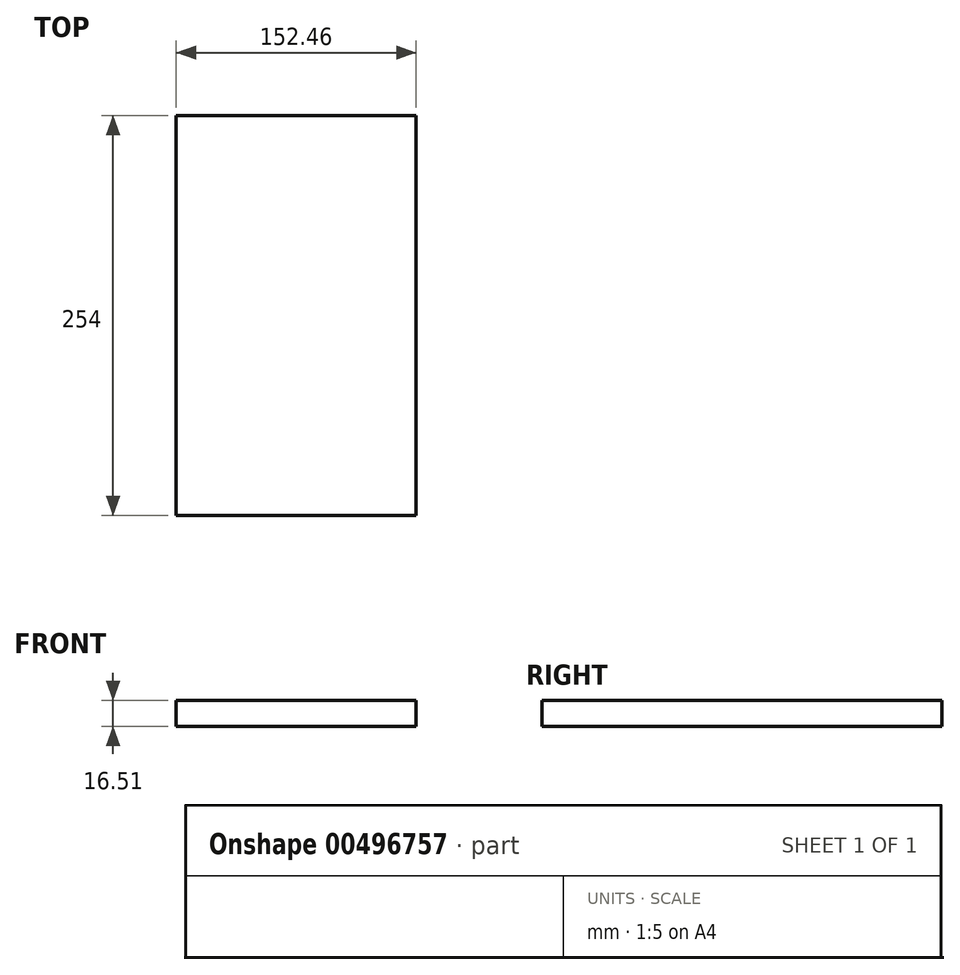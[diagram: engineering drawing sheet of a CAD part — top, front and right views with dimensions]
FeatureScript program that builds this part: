
annotation { "Feature Type Name" : "Feature", "Feature Type Description" : "" }
export const myFeature = defineFeature(function(context is Context, id is Id, definition is map)
    precondition{}
    {
        {
            var Q0;
            Q0=qCreatedBy(makeId("Front.planeOp"),FACE);
            var sketch = newSketch(context, id + "F0", { "sketchPlane" : qUnion([Q0])});
            skLineSegment(sketch, "E0", {"start": v(-76.65, 0) * mm, "end": v(-76.65, 16.5) * mm});
            skLineSegment(sketch, "E1", {"start": v(-76.65, 16.5) * mm, "end": v(75.81, 16.5) * mm});
            skLineSegment(sketch, "E2", {"start": v(75.81, 16.5) * mm, "end": v(75.81, 0) * mm});
            skLineSegment(sketch, "E3", {"start": v(75.81, 0) * mm, "end": v(-76.65, 0) * mm});
            skSolve(sketch);
        }
        {
            var Q0;
            Q0=makeQuery(id+"F0.imprint","IMPRINT",FACE,{"disambiguationData":[TD([[makeQuery(id+"F0.imprint","IMPRINT",EDGE,{"derivedFrom":sQuery(id+"F0.wireOp",EDGE,"E0")}),-1.0]])]});
            extrude(context, id + "F1", {"entities" : qUnion([Q0]), "depth" : 254 * mm});
        }
    });
